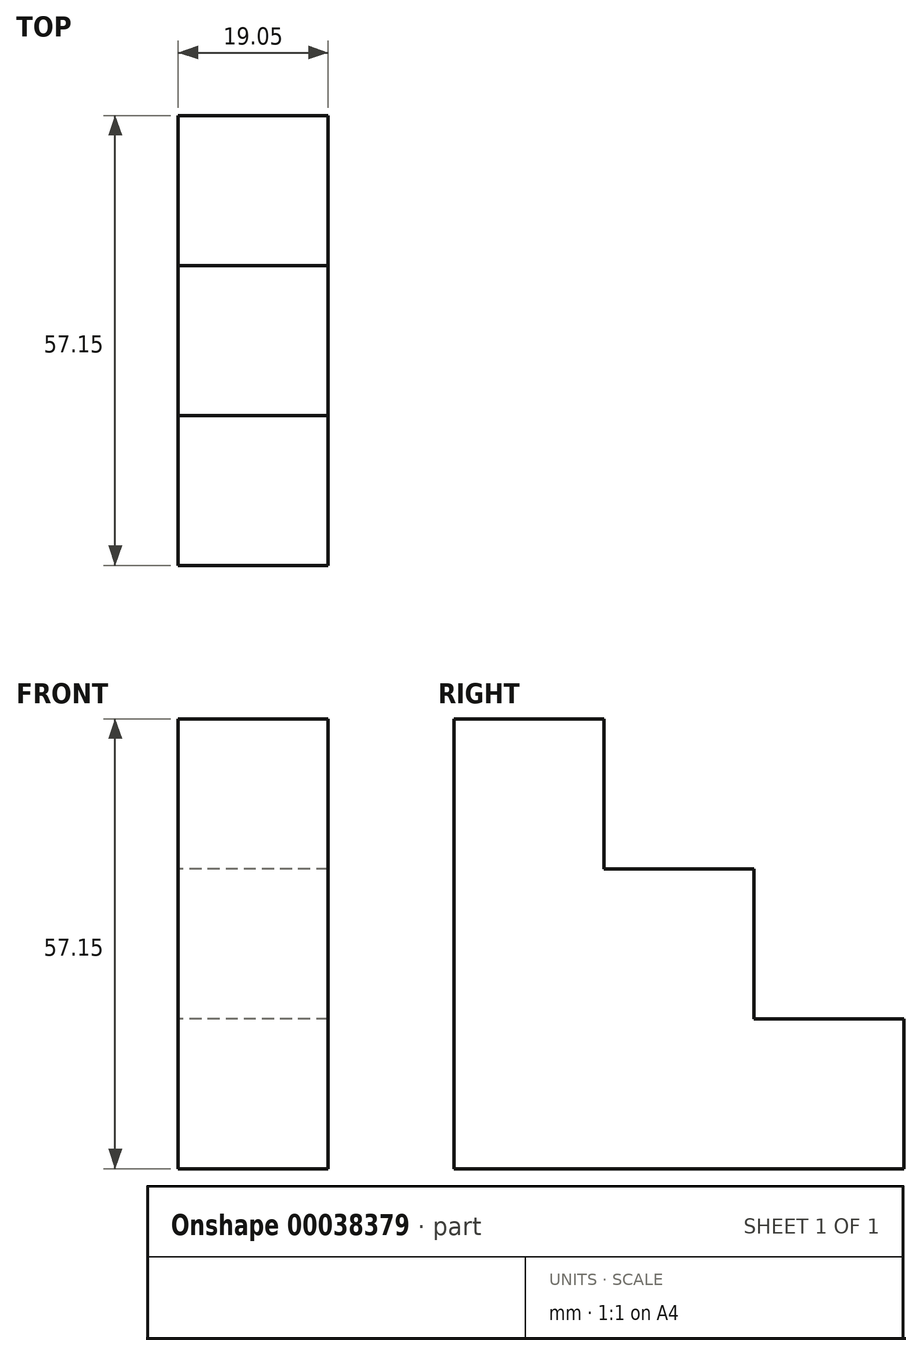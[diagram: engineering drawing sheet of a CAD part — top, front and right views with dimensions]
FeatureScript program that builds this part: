
annotation { "Feature Type Name" : "Feature", "Feature Type Description" : "" }
export const myFeature = defineFeature(function(context is Context, id is Id, definition is map)
    precondition{}
    {
        {
            var Q0;
            Q0=qCreatedBy(makeId("Top.planeOp"),FACE);
            var sketch = newSketch(context, id + "F0", { "sketchPlane" : qUnion([Q0])});
            skLineSegment(sketch, "E0.bottom", {"start": v(0, 0) * mm, "end": v(19.05, 0) * mm});
            skLineSegment(sketch, "E0.top", {"start": v(0, 19.05) * mm, "end": v(19.05, 19.05) * mm});
            skLineSegment(sketch, "E0.left", {"start": v(0, 0) * mm, "end": v(0, 19.05) * mm});
            skLineSegment(sketch, "E0.right", {"start": v(19.05, 0) * mm, "end": v(19.05, 19.05) * mm});
            skSolve(sketch);
        }
        {
            var Q0;
            Q0=makeQuery(id+"F0.imprint","IMPRINT",FACE,{"disambiguationData":[TD([[makeQuery(id+"F0.imprint","IMPRINT",EDGE,{"derivedFrom":sQuery(id+"F0.wireOp",EDGE,"E0.bottom")}),1.0]])]});
            extrude(context, id + "F1", {"entities" : qUnion([Q0]), "depth" : 19.05 * mm});
        }
        {
            var Q0;
            Q0=makeQuery(id+"F1.opExtrude","SWEPT_FACE",FACE,{"disambiguationData":[OSD([sQuery(id+"F0.wireOp",EDGE,"E0.top")])]});
            extrude(context, id + "F2", {"entities" : qUnion([Q0]), "operationType" : NewBodyOperationType.ADD, "depth" : 19.05 * mm});
        }
        {
            var Q0;
            {var subQ0=sQuery(id+"F0.wireOp",EDGE,"E0.top");Q0=makeQuery(id+"F2.boolean.opBoolean","MERGE",FACE,{"derivedFrom":[makeQuery(id+"F1.opExtrude","CAP_FACE",FACE,{"disambiguationData":[OSD([sQuery(id+"F0.wireOp",EDGE,"E0.bottom"),subQ0,sQuery(id+"F0.wireOp",EDGE,"E0.left"),sQuery(id+"F0.wireOp",EDGE,"E0.right")])],"isStart":false}),makeQuery(id+"F2.opExtrude","SWEPT_FACE",FACE,{"disambiguationData":[OSD([subQ0]),TDD([makeQuery(id+"F1.opExtrude","CAP_EDGE",EDGE,{"disambiguationData":[OSD([subQ0])],"isStart":false})])]})]});}
            var sketch = newSketch(context, id + "F3", { "sketchPlane" : qUnion([Q0])});
            skLineSegment(sketch, "E1.bottom", {"start": v(19.05, 19.05) * mm, "end": v(0, 19.05) * mm});
            skLineSegment(sketch, "E1.top", {"start": v(19.05, 0) * mm, "end": v(0, 0) * mm});
            skLineSegment(sketch, "E1.left", {"start": v(19.05, 19.05) * mm, "end": v(19.05, 0) * mm});
            skLineSegment(sketch, "E1.right", {"start": v(0, 19.05) * mm, "end": v(0, 0) * mm});
            skLineSegment(sketch, "E2.top", {"start": v(19.05, 38.1) * mm, "end": v(0, 38.1) * mm});
            skLineSegment(sketch, "E2.left", {"start": v(19.05, 19.05) * mm, "end": v(19.05, 38.1) * mm});
            skLineSegment(sketch, "E2.right", {"start": v(0, 19.05) * mm, "end": v(0, 38.1) * mm});
            skSolve(sketch);
        }
        {
            var Q0;
            Q0=makeQuery(id+"F2.opExtrude","CAP_FACE",FACE,{"disambiguationData":[OSD([sQuery(id+"F0.wireOp",EDGE,"E0.top")])],"isStart":false});
            extrude(context, id + "F4", {"entities" : qUnion([Q0]), "operationType" : NewBodyOperationType.ADD, "depth" : 19.05 * mm});
        }
        {
            var Q0;
            Q0=makeQuery(id+"F3.imprint","IMPRINT",FACE,{"disambiguationData":[TD([[makeQuery(id+"F3.imprint","IMPRINT",EDGE,{"derivedFrom":sQuery(id+"F3.wireOp",EDGE,"E1.top")}),1.0]])]});
            extrude(context, id + "F5", {"entities" : qUnion([Q0]), "operationType" : NewBodyOperationType.ADD, "depth" : 19.05 * mm});
        }
        {
            var Q0;
            Q0=makeQuery(id+"F5.opExtrude","CAP_FACE",FACE,{"disambiguationData":[OSD([sQuery(id+"F3.wireOp",EDGE,"E1.top"),sQuery(id+"F3.wireOp",EDGE,"E1.left"),sQuery(id+"F3.wireOp",EDGE,"E1.right"),sQuery(id+"F3.wireOp",EDGE,"E1.bottom")])],"isStart":false});
            extrude(context, id + "F6", {"entities" : qUnion([Q0]), "operationType" : NewBodyOperationType.ADD, "depth" : 19.05 * mm});
        }
        {
            var Q0;
            {var subQ0=sQuery(id+"F3.wireOp",EDGE,"E1.bottom");Q0=makeQuery(id+"F6.boolean.opBoolean","MERGE",FACE,{"derivedFrom":[makeQuery(id+"F5.opExtrude","SWEPT_FACE",FACE,{"disambiguationData":[OSD([subQ0])]}),makeQuery(id+"F6.opExtrude","SWEPT_FACE",FACE,{"disambiguationData":[OSD([subQ0])]})]});}
            var sketch = newSketch(context, id + "F7", { "sketchPlane" : qUnion([Q0])});
            skLineSegment(sketch, "E3.bottom", {"start": v(-19.05, 38.1) * mm, "end": v(0, 38.1) * mm});
            skLineSegment(sketch, "E3.top", {"start": v(-19.05, 19.05) * mm, "end": v(0, 19.05) * mm});
            skLineSegment(sketch, "E3.left", {"start": v(-19.05, 38.1) * mm, "end": v(-19.05, 19.05) * mm});
            skLineSegment(sketch, "E3.right", {"start": v(0, 38.1) * mm, "end": v(0, 19.05) * mm});
            skSolve(sketch);
        }
        {
            var Q0;
            Q0=makeQuery(id+"F7.imprint","IMPRINT",FACE,{"disambiguationData":[TD([[makeQuery(id+"F7.imprint","IMPRINT",EDGE,{"derivedFrom":sQuery(id+"F7.wireOp",EDGE,"E3.bottom")}),-1.0]])]});
            extrude(context, id + "F8", {"entities" : qUnion([Q0]), "operationType" : NewBodyOperationType.ADD, "depth" : 19.05 * mm});
        }
    });
